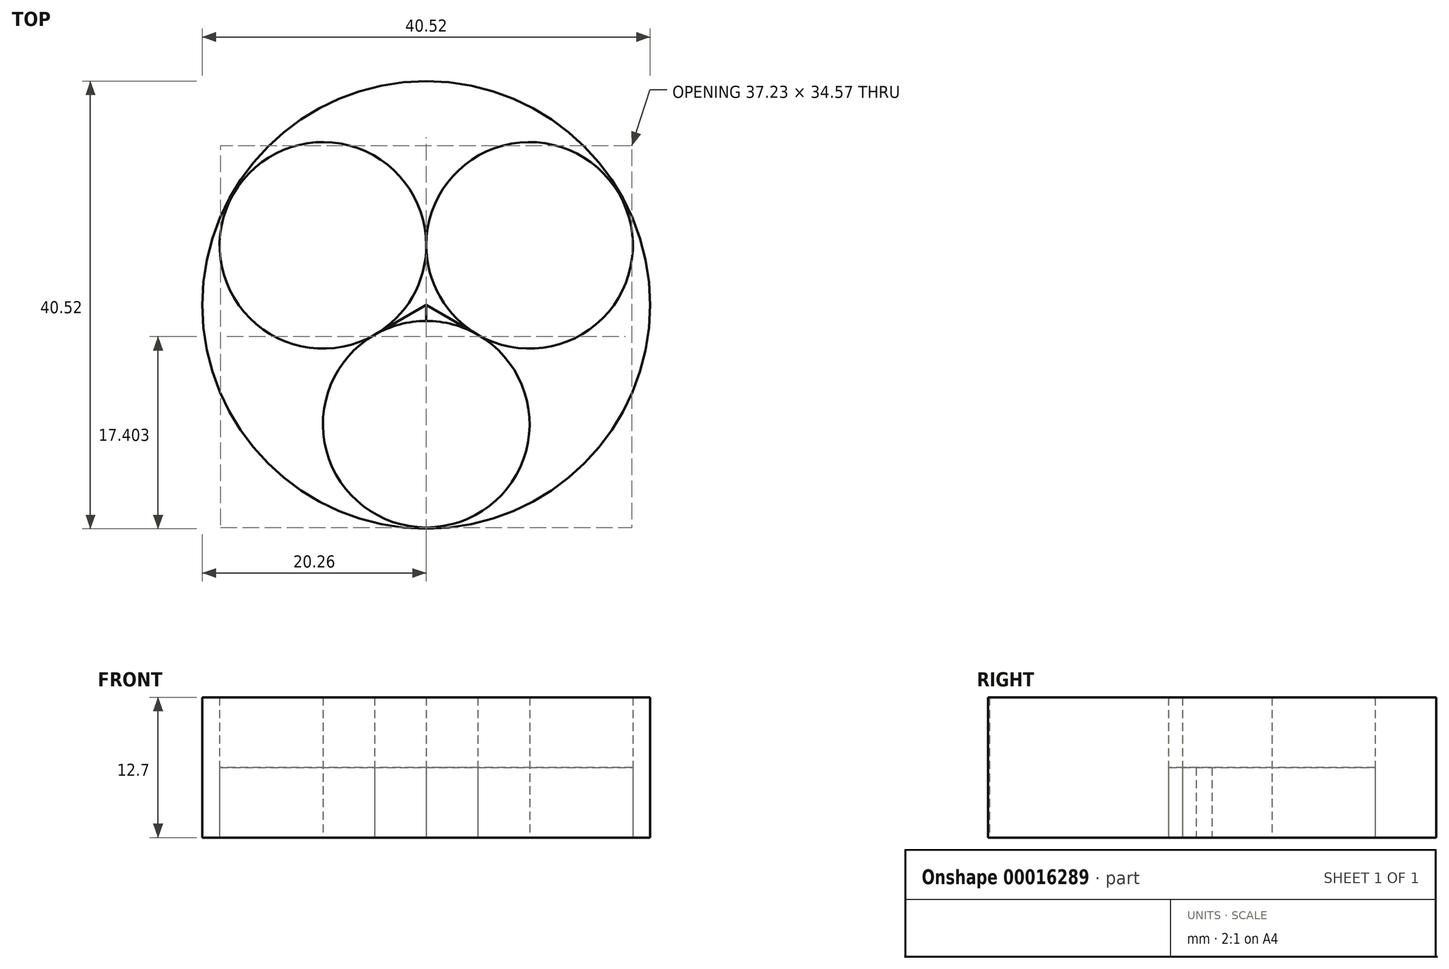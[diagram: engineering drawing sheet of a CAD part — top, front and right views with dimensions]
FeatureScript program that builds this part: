
annotation { "Feature Type Name" : "Feature", "Feature Type Description" : "" }
export const myFeature = defineFeature(function(context is Context, id is Id, definition is map)
    precondition{}
    {
        {
            var Q0;
            Q0=qCreatedBy(makeId("Top.planeOp"),FACE);
            var sketch = newSketch(context, id + "F0", { "sketchPlane" : qUnion([Q0])});
            skCircle(sketch, "E0", {"center": v(0, 0) * mm, "radius": 20.79 * mm});
            skCircle(sketch, "E1", {"center": v(0, 0) * mm, "radius": 20.26 * mm});
            skLineSegment(sketch, "E2", {"start": v(0, 0) * mm, "end": v(0, 20.79) * mm});
            skLineSegment(sketch, "E3", {"start": v(0, 0) * mm, "end": v(-18, -10.4) * mm});
            skLineSegment(sketch, "E4.MirrorCS", {"start": v(0, 0) * mm, "end": v(18, -10.4) * mm});
            skLineSegment(sketch, "E5", {"start": v(0, 0) * mm, "end": v(0, -20.79) * mm});
            skCircle(sketch, "E6", {"center": v(0, -10.8) * mm, "radius": 9.35 * mm});
            skCircle(sketch, "E7.MirrorC", {"center": v(9.35, 5.4) * mm, "radius": 9.35 * mm});
            skCircle(sketch, "E8.MirrorC", {"center": v(-9.35, 5.4) * mm, "radius": 9.35 * mm});
            skSolve(sketch);
        }
        {
            var Q0;
            {var subQ1=sQuery(id+"F0.wireOp",EDGE,"E3");var subQ5=sQuery(id+"F0.wireOp",EDGE,"E1");var subQ6=makeQuery(id+"F0.imprint","INTERSECT",VERTEX,{"derivedFrom":[subQ5,subQ1]});Q0=makeQuery(id+"F0.imprint","IMPRINT",FACE,{"disambiguationData":[TD([[makeQuery(id+"F0.imprint","IMPRINT",EDGE,{"disambiguationData":[TD([[subQ6,1.0]])],"derivedFrom":subQ5}),1.0]])]});}
            var Q1;
            {var subQ3=sQuery(id+"F0.wireOp",EDGE,"E2");var subQ5=sQuery(id+"F0.wireOp",EDGE,"E1");var subQ7=makeQuery(id+"F0.imprint","INTERSECT",VERTEX,{"derivedFrom":[subQ5,subQ3]});Q1=makeQuery(id+"F0.imprint","IMPRINT",FACE,{"disambiguationData":[TD([[makeQuery(id+"F0.imprint","IMPRINT",EDGE,{"disambiguationData":[TD([[subQ7,1.0]])],"derivedFrom":subQ5}),1.0]])]});}
            var Q2;
            {var subQ3=sQuery(id+"F0.wireOp",EDGE,"E5");var subQ5=sQuery(id+"F0.wireOp",EDGE,"E1");var subQ6=makeQuery(id+"F0.imprint","INTERSECT",VERTEX,{"derivedFrom":[subQ5,subQ3]});Q2=makeQuery(id+"F0.imprint","IMPRINT",FACE,{"disambiguationData":[TD([[makeQuery(id+"F0.imprint","IMPRINT",EDGE,{"disambiguationData":[TD([[subQ6,-1.0]])],"derivedFrom":subQ5}),1.0]])]});}
            var Q3;
            {var subQ1=sQuery(id+"F0.wireOp",EDGE,"E3");var subQ5=sQuery(id+"F0.wireOp",EDGE,"E1");var subQ7=makeQuery(id+"F0.imprint","INTERSECT",VERTEX,{"derivedFrom":[subQ5,subQ1]});Q3=makeQuery(id+"F0.imprint","IMPRINT",FACE,{"disambiguationData":[TD([[makeQuery(id+"F0.imprint","IMPRINT",EDGE,{"disambiguationData":[TD([[subQ7,-1.0]])],"derivedFrom":subQ5}),1.0]])]});}
            extrude(context, id + "F1", {"entities" : qUnion([Q0, Q1, Q2, Q3]), "depth" : 12.7 * mm});
        }
        {
            var Q0;
            {var subQ0=sQuery(id+"F0.wireOp",EDGE,"E8.MirrorC");var subQ3=sQuery(id+"F0.wireOp",EDGE,"E2");var subQ4=makeQuery(id+"F0.imprint","INTERSECT",VERTEX,{"derivedFrom":[subQ3,sQuery(id+"F0.wireOp",EDGE,"E7.MirrorC"),subQ0]});Q0=makeQuery(id+"F0.imprint","IMPRINT",FACE,{"disambiguationData":[TD([[makeQuery(id+"F0.imprint","IMPRINT",EDGE,{"disambiguationData":[TD([[subQ4,-1.0]])],"derivedFrom":subQ0}),1.0]])]});}
            var Q1;
            {var subQ0=sQuery(id+"F0.wireOp",EDGE,"E7.MirrorC");var subQ3=sQuery(id+"F0.wireOp",EDGE,"E2");var subQ4=makeQuery(id+"F0.imprint","INTERSECT",VERTEX,{"derivedFrom":[subQ3,subQ0,sQuery(id+"F0.wireOp",EDGE,"E8.MirrorC")]});Q1=makeQuery(id+"F0.imprint","IMPRINT",FACE,{"disambiguationData":[TD([[makeQuery(id+"F0.imprint","IMPRINT",EDGE,{"disambiguationData":[TD([[subQ4,1.0]])],"derivedFrom":subQ0}),1.0]])]});}
            var Q2;
            {var subQ0=sQuery(id+"F0.wireOp",EDGE,"E5");var subQ1=sQuery(id+"F0.wireOp",EDGE,"E6");var subQ2=makeQuery(id+"F0.imprint","INTERSECT",VERTEX,{"disambiguationData":[OD(0.0)],"derivedFrom":[subQ0,subQ1]});Q2=makeQuery(id+"F0.imprint","IMPRINT",FACE,{"disambiguationData":[TD([[makeQuery(id+"F0.imprint","IMPRINT",EDGE,{"disambiguationData":[TD([[subQ2,1.0]])],"derivedFrom":subQ1}),-1.0]])]});}
            var Q3;
            {var subQ0=sQuery(id+"F0.wireOp",EDGE,"E6");var subQ3=sQuery(id+"F0.wireOp",EDGE,"E5");var subQ4=makeQuery(id+"F0.imprint","INTERSECT",VERTEX,{"disambiguationData":[OD(0.0)],"derivedFrom":[subQ3,subQ0]});Q3=makeQuery(id+"F0.imprint","IMPRINT",FACE,{"disambiguationData":[TD([[makeQuery(id+"F0.imprint","IMPRINT",EDGE,{"disambiguationData":[TD([[subQ4,-1.0]])],"derivedFrom":subQ0}),-1.0]])]});}
            extrude(context, id + "F2", {"entities" : qUnion([Q0, Q1, Q2, Q3]), "depth" : 6.35 * mm});
        }
    });
